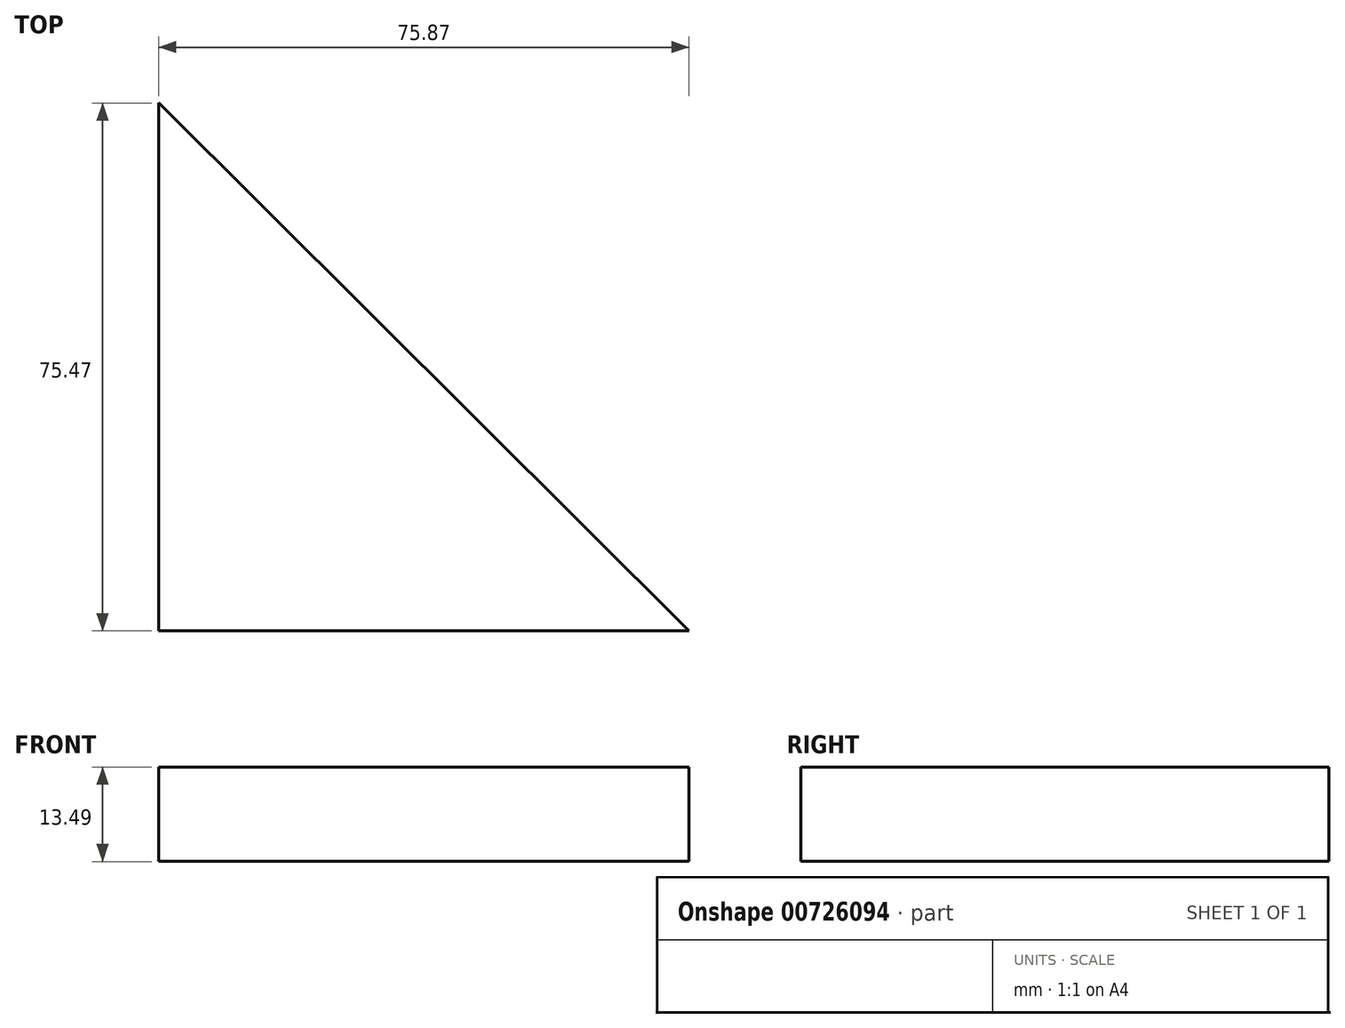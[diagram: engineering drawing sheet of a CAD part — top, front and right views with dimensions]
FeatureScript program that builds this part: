
annotation { "Feature Type Name" : "Feature", "Feature Type Description" : "" }
export const myFeature = defineFeature(function(context is Context, id is Id, definition is map)
    precondition{}
    {
        {
            var Q0;
            Q0=qCreatedBy(makeId("Top.planeOp"),FACE);
            var sketch = newSketch(context, id + "F0", { "sketchPlane" : qUnion([Q0])});
            skLineSegment(sketch, "E0", {"start": v(75.87, 0) * mm, "end": v(0, 0) * mm});
            skLineSegment(sketch, "E1", {"start": v(0, 0) * mm, "end": v(0, -72.6) * mm});
            skLineSegment(sketch, "E2", {"start": v(0, -72.6) * mm, "end": v(75.87, 0) * mm});
            skLineSegment(sketch, "E3", {"start": v(0, 75.47) * mm, "end": v(0, 0) * mm});
            skLineSegment(sketch, "E4", {"start": v(75.87, 0) * mm, "end": v(0, 75.47) * mm});
            skSolve(sketch);
        }
        {
            var Q0;
            Q0=makeQuery(id+"F0.imprint","IMPRINT",FACE,{"disambiguationData":[TD([[makeQuery(id+"F0.imprint","IMPRINT",EDGE,{"derivedFrom":sQuery(id+"F0.wireOp",EDGE,"E0")}),1.0]])]});
            var sketch = newSketch(context, id + "F1", { "sketchPlane" : qUnion([Q0])});
            skSolve(sketch);
        }
        {
            var Q0;
            Q0=makeQuery(id+"F0.imprint","IMPRINT",FACE,{"disambiguationData":[TD([[makeQuery(id+"F0.imprint","IMPRINT",EDGE,{"derivedFrom":sQuery(id+"F0.wireOp",EDGE,"E0")}),-1.0]])]});
            var Q1;
            Q1=makeQuery(id+"F1.imprint","IMPRINT",FACE,{"disambiguationData":[TD([[makeQuery(id+"F1.imprint","IMPRINT",EDGE,{"derivedFrom":makeQuery(id+"F0.imprint","IMPRINT",EDGE,{"derivedFrom":sQuery(id+"F0.wireOp",EDGE,"E0")})}),1.0]])]});
            extrude(context, id + "F2", {"entities" : qUnion([Q0, Q1]), "oppositeDirection" : true, "depth" : 13.5 * mm, "offsetDistance" : 25.4 * mm});
        }
    });
